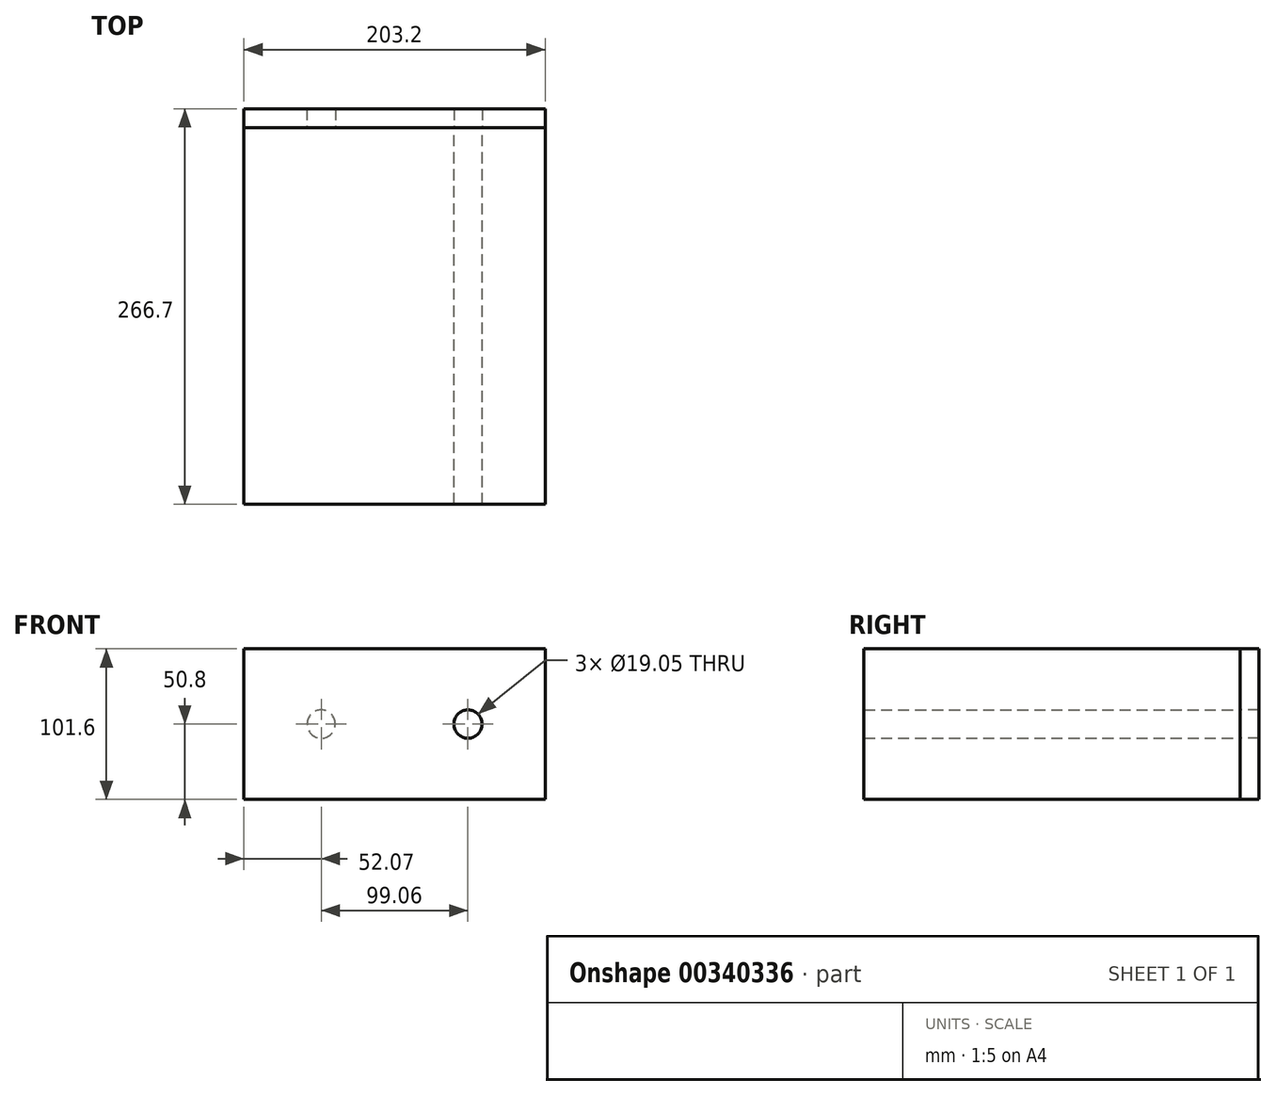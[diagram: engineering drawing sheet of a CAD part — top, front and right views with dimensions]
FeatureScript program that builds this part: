
annotation { "Feature Type Name" : "Feature", "Feature Type Description" : "" }
export const myFeature = defineFeature(function(context is Context, id is Id, definition is map)
    precondition{}
    {
        {
            var Q0;
            Q0=qCreatedBy(makeId("Front.planeOp"),FACE);
            var sketch = newSketch(context, id + "F0", { "sketchPlane" : qUnion([Q0])});
            skLineSegment(sketch, "E0.bottom", {"start": v(-101.6, 50.8) * mm, "end": v(101.6, 50.8) * mm});
            skLineSegment(sketch, "E0.top", {"start": v(-101.6, -50.8) * mm, "end": v(101.6, -50.8) * mm});
            skLineSegment(sketch, "E0.left", {"start": v(-101.6, 50.8) * mm, "end": v(-101.6, -50.8) * mm});
            skLineSegment(sketch, "E0.right", {"start": v(101.6, 50.8) * mm, "end": v(101.6, -50.8) * mm});
            skPoint(sketch, "E0.middle", {"position": v(0, 0) * mm});
            skCircle(sketch, "E1", {"center": v(-49.53, 0) * mm, "radius": 9.53 * mm});
            skLineSegment(sketch, "E2", {"start": v(0, -50.8) * mm, "end": v(0, 50.8) * mm, "construction": true});
            skCircle(sketch, "E3.MirrorC", {"center": v(49.53, 0) * mm, "radius": 9.53 * mm});
            skSolve(sketch);
        }
        {
            var Q0;
            Q0=makeQuery(id+"F0.imprint","IMPRINT",FACE,{"disambiguationData":[TD([[makeQuery(id+"F0.imprint","IMPRINT",EDGE,{"derivedFrom":sQuery(id+"F0.wireOp",EDGE,"E1")}),1.0]])]});
            var Q1;
            Q1=makeQuery(id+"F0.imprint","IMPRINT",FACE,{"disambiguationData":[TD([[makeQuery(id+"F0.imprint","IMPRINT",EDGE,{"derivedFrom":sQuery(id+"F0.wireOp",EDGE,"E3.MirrorC")}),-1.0]])]});
            extrude(context, id + "F1", {"entities" : qUnion([Q0, Q1]), "depth" : 254 * mm});
        }
        {
            var Q0;
            Q0=makeQuery(id+"F0.imprint","IMPRINT",FACE,{"disambiguationData":[TD([[makeQuery(id+"F0.imprint","IMPRINT",EDGE,{"derivedFrom":sQuery(id+"F0.wireOp",EDGE,"E0.bottom")}),-1.0]])]});
            extrude(context, id + "F2", {"entities" : qUnion([Q0]), "oppositeDirection" : true, "depth" : 12.7 * mm});
        }
    });
